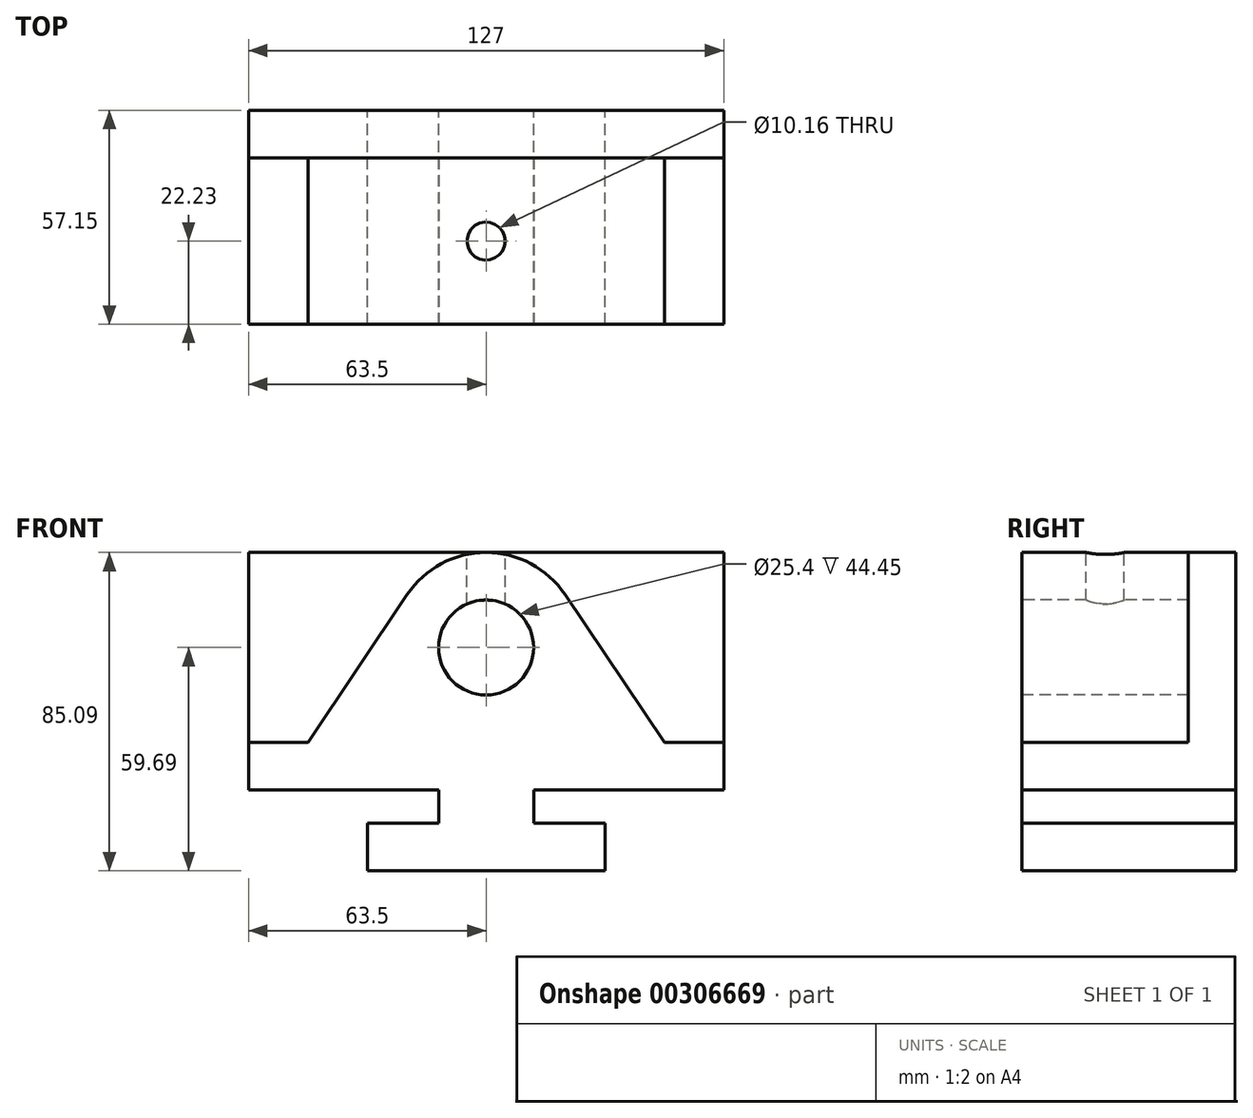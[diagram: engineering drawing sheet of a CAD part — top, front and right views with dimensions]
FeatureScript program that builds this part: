
annotation { "Feature Type Name" : "Feature", "Feature Type Description" : "" }
export const myFeature = defineFeature(function(context is Context, id is Id, definition is map)
    precondition{}
    {
        {
            var Q0;
            Q0=qCreatedBy(makeId("Front.planeOp"),FACE);
            var sketch = newSketch(context, id + "F0", { "sketchPlane" : qUnion([Q0])});
            skLineSegment(sketch, "E0", {"start": v(0, 0) * mm, "end": v(-31.75, 0) * mm});
            skLineSegment(sketch, "E1", {"start": v(-31.75, 0) * mm, "end": v(-31.75, 12.7) * mm});
            skLineSegment(sketch, "E2", {"start": v(-31.75, 12.7) * mm, "end": v(-12.7, 12.7) * mm});
            skLineSegment(sketch, "E3", {"start": v(-12.7, 12.7) * mm, "end": v(-12.7, 21.59) * mm});
            skLineSegment(sketch, "E4", {"start": v(-12.7, 21.59) * mm, "end": v(-63.5, 21.59) * mm});
            skLineSegment(sketch, "E5", {"start": v(-63.5, 21.59) * mm, "end": v(-63.5, 85.09) * mm});
            skLineSegment(sketch, "E6", {"start": v(-63.5, 85.09) * mm, "end": v(0, 85.09) * mm});
            skLineSegment(sketch, "E7.MirrorCS", {"start": v(31.75, 12.7) * mm, "end": v(12.7, 12.7) * mm});
            skLineSegment(sketch, "E8.MirrorCS", {"start": v(31.75, 0) * mm, "end": v(31.75, 12.7) * mm});
            skLineSegment(sketch, "E9.MirrorCS", {"start": v(63.5, 85.09) * mm, "end": v(0, 85.09) * mm});
            skLineSegment(sketch, "E10.MirrorCS", {"start": v(12.7, 21.59) * mm, "end": v(63.5, 21.59) * mm});
            skLineSegment(sketch, "E11.MirrorCS", {"start": v(12.7, 12.7) * mm, "end": v(12.7, 21.59) * mm});
            skLineSegment(sketch, "E12.MirrorCS", {"start": v(63.5, 21.59) * mm, "end": v(63.5, 85.09) * mm});
            skLineSegment(sketch, "E13.MirrorCS", {"start": v(0, 0) * mm, "end": v(31.75, 0) * mm});
            skSolve(sketch);
        }
        {
            var Q0;
            Q0=makeQuery(id+"F0.imprint","IMPRINT",FACE,{"disambiguationData":[TD([[makeQuery(id+"F0.imprint","IMPRINT",EDGE,{"derivedFrom":sQuery(id+"F0.wireOp",EDGE,"E0")}),-1.0]])]});
            extrude(context, id + "F1", {"entities" : qUnion([Q0]), "endBound" : BoundingType.SYMMETRIC, "depth" : 57.15 * mm});
        }
        {
            var Q0;
            Q0=makeQuery(id+"F1.opExtrude","CAP_FACE",FACE,{"disambiguationData":[OSD([sQuery(id+"F0.wireOp",EDGE,"E0"),sQuery(id+"F0.wireOp",EDGE,"E1"),sQuery(id+"F0.wireOp",EDGE,"E2"),sQuery(id+"F0.wireOp",EDGE,"E3"),sQuery(id+"F0.wireOp",EDGE,"E4"),sQuery(id+"F0.wireOp",EDGE,"E5"),sQuery(id+"F0.wireOp",EDGE,"E6"),sQuery(id+"F0.wireOp",EDGE,"E7.MirrorCS"),sQuery(id+"F0.wireOp",EDGE,"E8.MirrorCS"),sQuery(id+"F0.wireOp",EDGE,"E9.MirrorCS"),sQuery(id+"F0.wireOp",EDGE,"E10.MirrorCS"),sQuery(id+"F0.wireOp",EDGE,"E11.MirrorCS"),sQuery(id+"F0.wireOp",EDGE,"E12.MirrorCS"),sQuery(id+"F0.wireOp",EDGE,"E13.MirrorCS")])],"isStart":false});
            var sketch = newSketch(context, id + "F2", { "sketchPlane" : qUnion([Q0])});
            skLineSegment(sketch, "E14.0.0", {"start": v(31.75, 0) * mm, "end": v(31.75, 12.7) * mm});
            skLineSegment(sketch, "E14.0.1", {"start": v(31.75, 12.7) * mm, "end": v(12.7, 12.7) * mm});
            skLineSegment(sketch, "E14.0.2", {"start": v(12.7, 12.7) * mm, "end": v(12.7, 21.59) * mm});
            skLineSegment(sketch, "E14.0.3", {"start": v(12.7, 21.59) * mm, "end": v(63.5, 21.59) * mm});
            skLineSegment(sketch, "E14.0.4", {"start": v(63.5, 21.59) * mm, "end": v(63.5, 85.09) * mm});
            skLineSegment(sketch, "E14.0.5", {"start": v(63.5, 85.09) * mm, "end": v(-63.5, 85.09) * mm});
            skLineSegment(sketch, "E14.0.6", {"start": v(-63.5, 85.09) * mm, "end": v(-63.5, 21.59) * mm});
            skLineSegment(sketch, "E14.0.7", {"start": v(-63.5, 21.59) * mm, "end": v(-12.7, 21.59) * mm});
            skLineSegment(sketch, "E14.0.8", {"start": v(-12.7, 21.59) * mm, "end": v(-12.7, 12.7) * mm});
            skLineSegment(sketch, "E14.0.9", {"start": v(-12.7, 12.7) * mm, "end": v(-31.75, 12.7) * mm});
            skLineSegment(sketch, "E14.0.10", {"start": v(-31.75, 12.7) * mm, "end": v(-31.75, 0) * mm});
            skLineSegment(sketch, "E14.0.11", {"start": v(-31.75, 0) * mm, "end": v(31.75, 0) * mm});
            skLineSegment(sketch, "E15", {"start": v(0, 0) * mm, "end": v(0, 85.09) * mm, "construction": true});
            skLineSegment(sketch, "E16", {"start": v(-63.5, 21.59) * mm, "end": v(-63.5, 34.3) * mm});
            skLineSegment(sketch, "E17", {"start": v(-63.5, 34.3) * mm, "end": v(-47.62, 34.3) * mm});
            skLineSegment(sketch, "E18", {"start": v(63.5, 21.59) * mm, "end": v(63.5, 34.3) * mm});
            skLineSegment(sketch, "E19", {"start": v(63.5, 34.3) * mm, "end": v(47.62, 34.3) * mm});
            skCircle(sketch, "E20", {"center": v(0, 59.69) * mm, "radius": 25.4 * mm});
            skLineSegment(sketch, "E21", {"start": v(-47.62, 34.3) * mm, "end": v(-21.1, 73.84) * mm});
            skLineSegment(sketch, "E22", {"start": v(47.62, 34.3) * mm, "end": v(21.1, 73.84) * mm});
            skSolve(sketch);
        }
        {
            var Q0;
            {var subQ4=sQuery(id+"F2.wireOp",EDGE,"E14.0.6");Q0=makeQuery(id+"F2.imprint","IMPRINT",FACE,{"disambiguationData":[TD([[makeQuery(id+"F2.imprint","IMPRINT",EDGE,{"derivedFrom":subQ4}),-1.0]])]});}
            var Q1;
            {var subQ4=sQuery(id+"F2.wireOp",EDGE,"E14.0.4");Q1=makeQuery(id+"F2.imprint","IMPRINT",FACE,{"disambiguationData":[TD([[makeQuery(id+"F2.imprint","IMPRINT",EDGE,{"derivedFrom":subQ4}),1.0]])]});}
            extrude(context, id + "F3", {"entities" : qUnion([Q0, Q1]), "operationType" : NewBodyOperationType.REMOVE, "oppositeDirection" : true, "depth" : 44.45 * mm});
        }
        {
            var Q0;
            Q0=makeQuery(id+"F1.opExtrude","CAP_FACE",FACE,{"disambiguationData":[OSD([sQuery(id+"F0.wireOp",EDGE,"E0"),sQuery(id+"F0.wireOp",EDGE,"E1"),sQuery(id+"F0.wireOp",EDGE,"E2"),sQuery(id+"F0.wireOp",EDGE,"E3"),sQuery(id+"F0.wireOp",EDGE,"E4"),sQuery(id+"F0.wireOp",EDGE,"E5"),sQuery(id+"F0.wireOp",EDGE,"E6"),sQuery(id+"F0.wireOp",EDGE,"E7.MirrorCS"),sQuery(id+"F0.wireOp",EDGE,"E8.MirrorCS"),sQuery(id+"F0.wireOp",EDGE,"E9.MirrorCS"),sQuery(id+"F0.wireOp",EDGE,"E10.MirrorCS"),sQuery(id+"F0.wireOp",EDGE,"E11.MirrorCS"),sQuery(id+"F0.wireOp",EDGE,"E12.MirrorCS"),sQuery(id+"F0.wireOp",EDGE,"E13.MirrorCS")])],"isStart":false});
            var sketch = newSketch(context, id + "F4", { "sketchPlane" : qUnion([Q0])});
            skArc(sketch, "E23.0", {"start": v(21.1, 73.84) * mm, "mid": v(0, 85.09) * mm, "end": v(-21.1, 73.84) * mm});
            skCircle(sketch, "E24", {"center": v(0, 59.69) * mm, "radius": 12.7 * mm});
            skSolve(sketch);
        }
        {
            var Q0;
            Q0=makeQuery(id+"F4.imprint","IMPRINT",FACE,{"disambiguationData":[TD([[makeQuery(id+"F4.imprint","IMPRINT",EDGE,{"derivedFrom":sQuery(id+"F4.wireOp",EDGE,"E24")}),1.0]])]});
            extrude(context, id + "F5", {"entities" : qUnion([Q0]), "operationType" : NewBodyOperationType.REMOVE, "oppositeDirection" : true, "depth" : 44.45 * mm});
        }
        {
            var Q0;
            Q0=makeQuery(id+"F1.opExtrude","SWEPT_FACE",FACE,{"disambiguationData":[OSD([sQuery(id+"F0.wireOp",EDGE,"E6"),sQuery(id+"F0.wireOp",EDGE,"E9.MirrorCS")])]});
            var sketch = newSketch(context, id + "F6", { "sketchPlane" : qUnion([Q0])});
            skLineSegment(sketch, "E25.0.0", {"start": v(-21.1, -28.58) * mm, "end": v(21.1, -28.58) * mm});
            skLineSegment(sketch, "E25.0.1", {"start": v(21.1, -28.58) * mm, "end": v(21.1, 15.88) * mm});
            skLineSegment(sketch, "E25.0.2", {"start": v(21.1, 15.88) * mm, "end": v(0, 15.88) * mm});
            skLineSegment(sketch, "E25.0.3", {"start": v(0, 15.88) * mm, "end": v(-21.1, 15.88) * mm});
            skLineSegment(sketch, "E25.0.4", {"start": v(-21.1, 15.88) * mm, "end": v(-21.1, -28.58) * mm});
            skLineSegment(sketch, "E26", {"start": v(-21.1, -6.35) * mm, "end": v(21.1, -6.35) * mm, "construction": true});
            skCircle(sketch, "E27", {"center": v(0, -6.35) * mm, "radius": 5.08 * mm});
            skSolve(sketch);
        }
        {
            var Q0;
            Q0=makeQuery(id+"F6.imprint","IMPRINT",FACE,{"disambiguationData":[TD([[makeQuery(id+"F6.imprint","IMPRINT",EDGE,{"derivedFrom":sQuery(id+"F6.wireOp",EDGE,"E27")}),1.0]])]});
            extrude(context, id + "F7", {"entities" : qUnion([Q0]), "operationType" : NewBodyOperationType.REMOVE, "oppositeDirection" : true, "depth" : 25.4 * mm});
        }
    });
